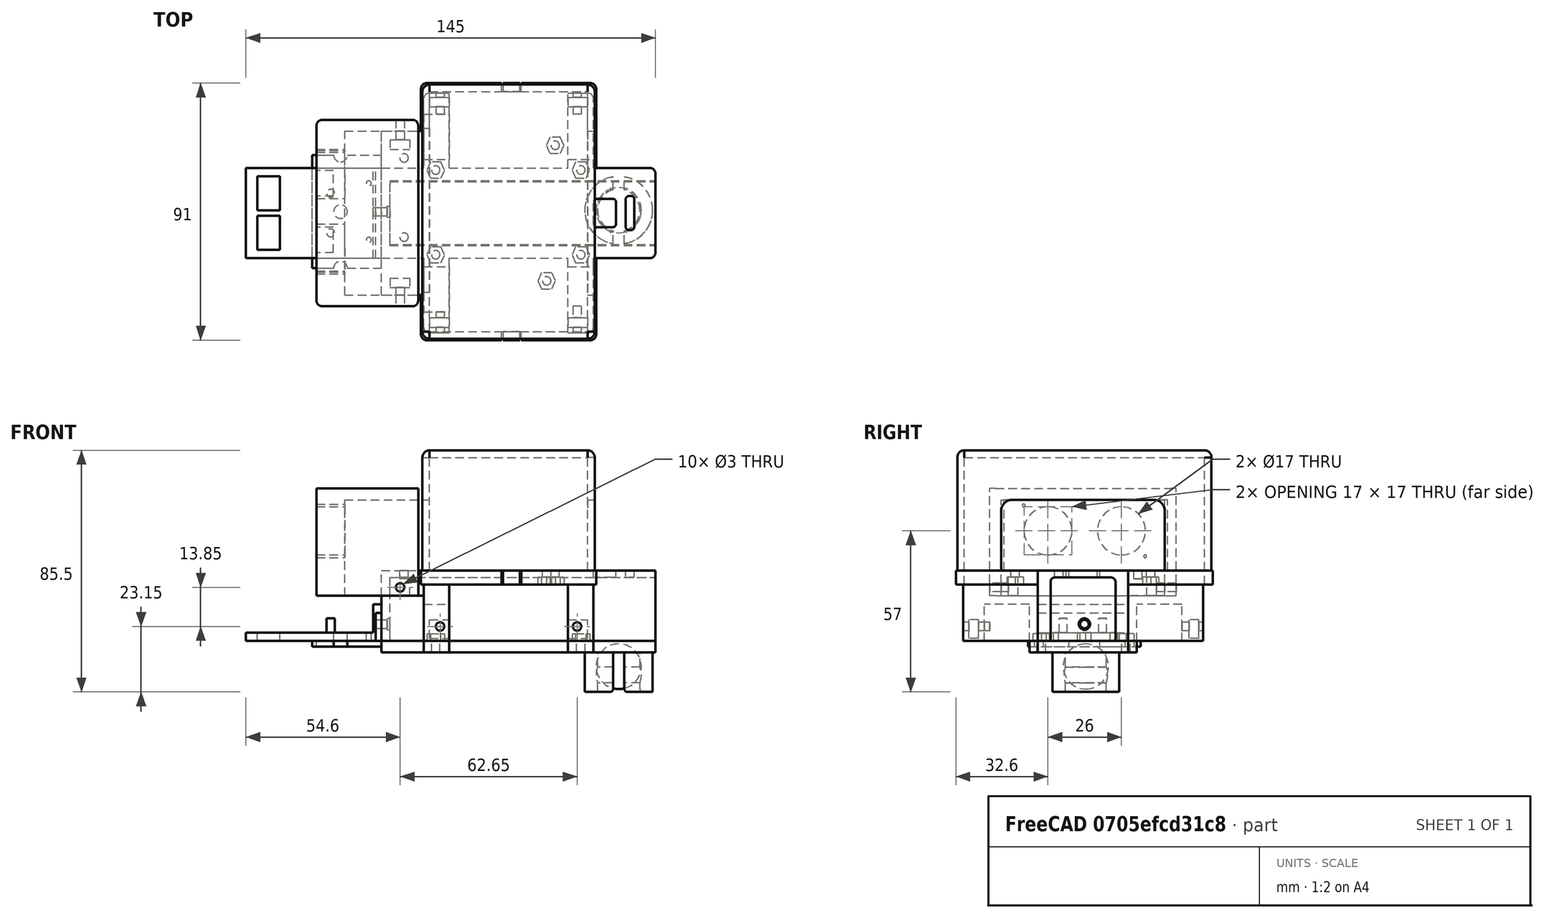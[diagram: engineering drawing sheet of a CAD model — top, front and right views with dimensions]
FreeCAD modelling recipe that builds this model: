
FCSTD DOCUMENT  (FreeCAD 0.14R3700 (Git))
Label: startRobot_v2
License: CC-BY 3.0
LicenseURL: http://creativecommons.org/licenses/by/3.0/
objects: Part::Cut×56, Part::Box×45, Part::Cylinder×33, Part::MultiFuse×15, Part::Fillet×9, Part::Offset×9, Mesh::Feature×7, PartDesign::Pad×7, Part::Feature×4, Part::Sphere×3, Part::Thickness×1, Sketcher::SketchObject×1
note: 190 computed .brp shape members not serialized (recipe doc carries the construction recipe); baked Part::Feature solids carry a one-line shape summary decoded from their .brp

FEATURE [Mesh::Feature] powerBank
  Placement = pos=(52,10,0) rot=(0,0,1;3.14159rad)
FEATURE [Part::Box] Box  label="Cubo"
  Height = 25
  Length = 94
  Placement = pos=(-42,-17,0) rot=(0,0,1;0rad)
  Width = 32
FEATURE [Part::Box] Box001  label="Cubo001"
  Height = 22
  Length = 94
  Placement = pos=(-42,-12,0) rot=(0,0,1;0rad)
  Width = 22
FEATURE [Part::Fillet] Fillet
  Base = -> Box001
  Edges = 4 edges r=1: [Edge9,Edge10,Edge11,Edge12]
FEATURE [Part::Offset] Offset
  Fill = false
  Intersection = false
  Join = 0
  Mode = 0
  SelfIntersection = false
  Source = -> Fillet
  Value = 0.5
FEATURE [Part::Cut] Cut
  Base = -> Box
  Tool = -> Offset
FEATURE [Part::Feature] futaba  label="Right-servo001"
  Placement = pos=(0,-17,10) rot=(0,0,1;0rad)
  shape: bbox 55.3 x 42 x 20 mm, 163 faces, 0 solids (baked)
FEATURE [Part::Feature] futaba001  label="Left-servo001"
  Placement = pos=(0,15,10) rot=(0,0,1;0rad)
  shape: bbox 55.3 x 42 x 20 mm, 163 faces, 0 solids (baked)
FEATURE [Part::Box] Box002  label="Cubo002"
  Height = 5
  Length = 62
  Placement = pos=(-31,-46,20) rot=(0,0,1;0rad)
  Width = 29
FEATURE [Part::Box] Box003  label="Cubo003"
  Height = 5
  Length = 62
  Placement = pos=(-31,15,20) rot=(0,0,1;0rad)
  Width = 30
FEATURE [Part::MultiFuse] Fusion
  Shapes = -> [Cut,Box002,Box003]
FEATURE [Part::Box] Box004  label="Cubo004"
  Height = 20
  Length = 9
  Placement = pos=(21,-43.4,0) rot=(0,0,1;0rad)
  Width = 27
FEATURE [Part::MultiFuse] Fusion001
  Shapes = -> [Fusion,Box004]
FEATURE [Part::Box] Box006  label="Cubo006"
  Height = 20
  Length = 9
  Placement = pos=(21,14.5,0) rot=(0,0,1;0rad)
  Width = 27
FEATURE [Part::MultiFuse] Fusion002
  Shapes = -> [Fusion001,Box006]
FEATURE [Part::Box] Box007  label="Cubo007"
  Height = 20
  Length = 9
  Placement = pos=(-30,14.5,0) rot=(0,0,1;0rad)
  Width = 27
FEATURE [Part::Box] Box008  label="Cubo008"
  Height = 20
  Length = 9
  Placement = pos=(-30,-43.4,0) rot=(0,0,1;0rad)
  Width = 27
FEATURE [Part::MultiFuse] Fusion003
  Shapes = -> [Fusion002,Box008]
FEATURE [Part::MultiFuse] Fusion004
  Shapes = -> [Fusion003,Box007]
FEATURE [Mesh::Feature] hc_sr  label="hc-sr04"
  Placement = pos=(-57,22,29) rot=(0.57735,-0.57735,-0.57735;2.0944rad)
FEATURE [Part::Box] Box010  label="Cubo010"
  Height = 25
  Length = 3
  Placement = pos=(-45,-17,0) rot=(0,0,1;0rad)
  Width = 32
FEATURE [Part::MultiFuse] Fusion005
  Shapes = -> [Box010,Fusion004]
FEATURE [Mesh::Feature] baseArduino
  Placement = pos=(-4,-1,30) rot=(0,0,1;1.5708rad)
FEATURE [Part::Box] Box011  label="Cubo011"
  Height = 4
  Length = 36
  Placement = pos=(-62,-34,50) rot=(0,0,1;0rad)
  Width = 66
FEATURE [Part::Box] Box012  label="Cubo012"
  Height = 34
  Length = 10
  Placement = pos=(-62,-34,16) rot=(0,0,1;0rad)
  Width = 66
FEATURE [Part::Box] Box013  label="Cubo013"
  Height = 9
  Length = 17
  Placement = pos=(-45,15,16) rot=(0,0,1;0rad)
  Width = 13
FEATURE [Part::Box] Box014  label="Cubo014"
  Height = 34
  Length = 26
  Placement = pos=(-52,28,16) rot=(0,0,1;0rad)
  Width = 4
FEATURE [Part::Box] Box015  label="huecoTuerca"
  Height = 3.4
  Length = 7
  Placement = pos=(-42,25,16) rot=(1,0,0;1.5708rad)
  Width = 6.5
FEATURE [Part::Box] Box016  label="huecoTuerca001"
  Height = 3.4
  Length = 7
  Placement = pos=(-28,40,1) rot=(1,0,0;1.5708rad)
  Width = 6.5
FEATURE [Part::Box] Box017  label="Cubo015"
  Height = 34
  Length = 26
  Placement = pos=(-52,-34,16) rot=(0,0,1;0rad)
  Width = 4
FEATURE [Part::Box] Box018  label="Cubo016"
  Height = 9
  Length = 17
  Placement = pos=(-45,-30,16) rot=(0,0,1;0rad)
  Width = 13
FEATURE [Part::Box] Box019  label="huecoTuerca002"
  Height = 3.4
  Length = 7
  Placement = pos=(-42,-24,16) rot=(1,0,0;1.5708rad)
  Width = 6.5
FEATURE [Part::MultiFuse] Fusion006  label="cabeza"
  Shapes = -> [Box011,Box012,Box014,Box017]
FEATURE [Part::MultiFuse] Fusion007
  Shapes = -> [Fusion005,Box013,Box018]
FEATURE [Part::Cut] Cut001
  Base = -> Fusion007
  Tool = -> Box015
FEATURE [Part::Cut] Cut002
  Base = -> Cut001
  Tool = -> Box019
FEATURE [Part::Box] Box020  label="huecoTuerca003"
  Height = 3.4
  Length = 7
  Placement = pos=(-28,-38,1) rot=(1,0,0;1.5708rad)
  Width = 6.5
FEATURE [Part::Cut] Cut003
  Base = -> Cut002
  Tool = -> Box016
FEATURE [Part::Cut] Cut004
  Base = -> Cut003
  Tool = -> Box020
FEATURE [Part::Box] Box021  label="huecoTuerca004"
  Height = 3.4
  Length = 7
  Placement = pos=(21,40,1) rot=(1,0,0;1.5708rad)
  Width = 6.5
FEATURE [Part::Box] Box022  label="huecoTuerca005"
  Height = 3.4
  Length = 7
  Placement = pos=(21,-38,1) rot=(1,0,0;1.5708rad)
  Width = 6.5
FEATURE [Part::Cut] Cut005
  Base = -> Cut004
  Tool = -> Box021
FEATURE [Part::Cut] Cut006
  Base = -> Cut005
  Tool = -> Box022
FEATURE [Part::Cylinder] Cylinder  label="Cilindro"
  Angle = 360
  Height = 10
  Placement = pos=(24.25,44,5.15) rot=(1,0,0;1.5708rad)
  Radius = 1.5
FEATURE [Part::Cylinder] Cylinder001  label="Cilindro001"
  Angle = 360
  Height = 10
  Placement = pos=(-24.25,44,5.15) rot=(1,0,0;1.5708rad)
  Radius = 1.5
FEATURE [Part::Cylinder] Cylinder002  label="Cilindro002"
  Angle = 360
  Height = 10
  Placement = pos=(24.25,-34,5.15) rot=(1,0,0;1.5708rad)
  Radius = 1.5
FEATURE [Part::Cylinder] Cylinder003  label="Cilindro003"
  Angle = 360
  Height = 10
  Placement = pos=(-24.25,-34,5.15) rot=(1,0,0;1.5708rad)
  Radius = 1.5
FEATURE [Part::Cut] Cut007
  Base = -> Cut006
  Tool = -> Cylinder
FEATURE [Part::Cut] Cut008
  Base = -> Cut007
  Tool = -> Cylinder001
FEATURE [Part::Cut] Cut009
  Base = -> Cut008
  Tool = -> Cylinder003
FEATURE [Part::Cut] Cut010
  Base = -> Cut009
  Tool = -> Cylinder002
FEATURE [Part::Box] Box023  label="Cubo017"
  Height = 13
  Length = 11
  Placement = pos=(-31,18,0) rot=(0,0,1;0rad)
  Width = 16
FEATURE [Part::Box] Box024  label="Cubo018"
  Height = 13
  Length = 11
  Placement = pos=(-31,-36,0) rot=(0,0,1;0rad)
  Width = 16
FEATURE [Part::Cut] Cut011
  Base = -> Cut010
  Tool = -> Box023
FEATURE [Part::Cut] Cut012
  Base = -> Cut011
  Tool = -> Box024
FEATURE [Part::Cylinder] Cylinder004  label="Cilindro004"
  Angle = 360
  Height = 10
  Placement = pos=(-38.4,-24,19) rot=(1,0,0;1.5708rad)
  Radius = 1.5
FEATURE [Part::Cylinder] Cylinder005  label="Cilindro005"
  Angle = 360
  Height = 10
  Placement = pos=(-38.4,32,19) rot=(1,0,0;1.5708rad)
  Radius = 1.5
FEATURE [Part::Cylinder] Cylinder006  label="Cilindro006"
  Angle = 360
  Height = 10
  Placement = pos=(-32.4,-24,19) rot=(1,0,0;1.5708rad)
  Radius = 1.5
FEATURE [Part::Cylinder] Cylinder007  label="Cilindro007"
  Angle = 360
  Height = 10
  Placement = pos=(-32.4,32,19) rot=(1,0,0;1.5708rad)
  Radius = 1.5
FEATURE [Part::Cut] Cut013
  Base = -> Cut012
  Tool = -> Cylinder004
FEATURE [Part::Cut] Cut014
  Base = -> Cut013
  Tool = -> Cylinder005
FEATURE [Part::Cut] Cut015
  Base = -> Fusion006
  Tool = -> Cylinder006
FEATURE [Part::Cut] Cut016
  Base = -> Cut015
  Tool = -> Cylinder007
FEATURE [Part::Box] Box025  label="Cubo019"
  Height = 4
  Length = 97
  Placement = pos=(-45,-17,-4) rot=(0,0,1;0rad)
  Width = 32
FEATURE [PartDesign::Pad] Pad  label="tuercaM015"
  Length = 2.4
  Length2 = 100
  Placement = pos=(-24.2,25,14.8) rot=(1,0,0;1.5708rad)
  Type = 0
FEATURE [Part::Offset] Offset001  label="tuercaM014"
  Fill = false
  Intersection = false
  Join = 2
  Mode = 0
  Placement = pos=(-1.6,-1,-22.5) rot=(1,0,0;1.5708rad)
  SelfIntersection = false
  Source = -> Pad
  Value = 0.1
FEATURE [PartDesign::Pad] Pad001  label="tuercaM017"
  Length = 2.4
  Length2 = 100
  Placement = pos=(-24.2,25,14.8) rot=(1,0,0;1.5708rad)
  Type = 0
FEATURE [Part::Offset] Offset002  label="tuercaM016"
  Fill = false
  Intersection = false
  Join = 2
  Mode = 0
  Placement = pos=(-1.6,29,-22.5) rot=(1,0,0;1.5708rad)
  SelfIntersection = false
  Source = -> Pad001
  Value = 0.1
FEATURE [Part::Cut] Cut017
  Base = -> Cut014
  Tool = -> Offset001
FEATURE [Part::Cut] Cut018
  Base = -> Cut017
  Tool = -> Offset002
FEATURE [Part::Box] Box026  label="Cubo020"
  Height = 4
  Length = 9
  Placement = pos=(-30,15,-4) rot=(0,0,1;0rad)
  Width = 3
FEATURE [Part::Box] Box027  label="Cubo021"
  Height = 4
  Length = 9
  Placement = pos=(-30,-20,-4) rot=(0,0,1;0rad)
  Width = 3
FEATURE [Part::MultiFuse] Fusion008
  Shapes = -> [Box025,Box026,Box027]
FEATURE [PartDesign::Pad] Pad002  label="tuercaM019"
  Length = 2.4
  Length2 = 100
  Placement = pos=(-24.2,25,14.8) rot=(1,0,0;1.5708rad)
  Type = 0
FEATURE [Part::Offset] Offset003  label="tuercaM018"
  Fill = false
  Intersection = false
  Join = 2
  Mode = 0
  Placement = pos=(49.8,29,-22.5) rot=(1,0,0;1.5708rad)
  SelfIntersection = false
  Source = -> Pad002
  Value = 0.1
FEATURE [PartDesign::Pad] Pad003  label="tuercaM021"
  Length = 2.4
  Length2 = 100
  Placement = pos=(-24.2,25,14.8) rot=(1,0,0;1.5708rad)
  Type = 0
FEATURE [Part::Offset] Offset004  label="tuercaM020"
  Fill = false
  Intersection = false
  Join = 2
  Mode = 0
  Placement = pos=(49.8,-1,-22.5) rot=(1,0,0;1.5708rad)
  SelfIntersection = false
  Source = -> Pad003
  Value = 0.1
FEATURE [Part::Cut] Cut019
  Base = -> Cut018
  Tool = -> Offset003
FEATURE [Part::Cut] Cut020
  Base = -> Cut019
  Tool = -> Offset004
FEATURE [Part::Box] Box028  label="Cubo022"
  Height = 4
  Length = 9
  Placement = pos=(21,15,-4) rot=(0,0,1;0rad)
  Width = 3
FEATURE [Part::Box] Box029  label="Cubo023"
  Height = 4
  Length = 9
  Placement = pos=(21,-20,-4) rot=(0,0,1;0rad)
  Width = 3
FEATURE [Part::MultiFuse] Fusion009
  Shapes = -> [Fusion008,Box028,Box029]
FEATURE [Part::Cylinder] Cylinder008  label="Cilindro008"
  Angle = 360
  Height = 6
  Placement = pos=(25.6,14.25,-4) rot=(0,0,1;0rad)
  Radius = 1.5
FEATURE [Part::Cylinder] Cylinder009  label="Cilindro009"
  Angle = 360
  Height = 6
  Placement = pos=(25.6,-15.75,-4) rot=(0,0,1;0rad)
  Radius = 1.5
FEATURE [Part::Cylinder] Cylinder010  label="Cilindro010"
  Angle = 360
  Height = 6
  Placement = pos=(-25.8,-15.75,-4) rot=(0,0,1;0rad)
  Radius = 1.5
FEATURE [Part::Cylinder] Cylinder011  label="Cilindro011"
  Angle = 360
  Height = 6
  Placement = pos=(-25.8,14.25,-4) rot=(0,0,1;0rad)
  Radius = 1.5
FEATURE [Part::Cut] Cut021
  Base = -> Fusion009
  Tool = -> Cylinder008
FEATURE [Part::Cut] Cut022
  Base = -> Cut021
  Tool = -> Cylinder011
FEATURE [Part::Cut] Cut023
  Base = -> Cut022
  Tool = -> Cylinder010
FEATURE [Part::Cut] Cut024  label="baseBateria"
  Base = -> Cut023
  Tool = -> Cylinder009
FEATURE [Part::Box] Box030  label="Cubo024"
  Height = 10
  Length = 8
  Placement = pos=(30,-6,19) rot=(0,0,1;0rad)
  Width = 10
FEATURE [Part::Fillet] Fillet001
  Base = -> Box030
  Edges = 4 edges r=1: [Edge1,Edge3,Edge5,Edge7]
FEATURE [Part::Box] Box031  label="Cubo025"
  Height = 10
  Length = 3
  Placement = pos=(41.5,-7,20) rot=(0,0,1;0rad)
  Width = 12
FEATURE [Part::Fillet] Fillet002
  Base = -> Box031
  Edges = 4 edges r=1: [Edge1,Edge3,Edge5,Edge7]
FEATURE [Part::Cut] Cut025
  Base = -> Cut020
  Tool = -> Fillet001
FEATURE [Part::Cut] Cut026
  Base = -> Cut025
  Tool = -> Fillet002
FEATURE [Part::Fillet] Fillet003
  Base = -> Cut026
  Edges = 10 edges r=2: [Edge86,Edge87,Edge180,Edge190,Edge231,Edge243,Edge350,Edge351,Edge352,Edge353]
FEATURE [Part::Feature] Servo_wheel_4_arm_horn  label="Servo_wheel_4_arm_horn003"
  Placement = pos=(1,-17,10) rot=(0,0,1;0rad)
  shape: bbox 56 x 6 x 56 mm, 1285 faces, 0 solids (baked)
FEATURE [Part::Feature] Servo_wheel_4_arm_horn001  label="Servo_wheel_4_arm_horn004"
  Placement = pos=(0,14,10) rot=(0,0,1;0rad)
  shape: bbox 56 x 6 x 56 mm, 1286 faces, 0 solids (baked)
FEATURE [PartDesign::Pad] Pad004  label="tuercaM023"
  Length = 2.4
  Length2 = 100
  Placement = pos=(-24.2,25,14.8) rot=(1,0,0;1.5708rad)
  Type = 0
FEATURE [Part::Offset] Offset005  label="tuercaM022"
  Fill = false
  Intersection = false
  Join = 2
  Mode = 0
  Placement = pos=(37.7,-10.2,-2.5) rot=(1,0,0;1.5708rad)
  SelfIntersection = false
  Source = -> Pad004
  Value = 0.1
FEATURE [Part::Cylinder] Cylinder013  label="Cilindro013"
  Angle = 360
  Height = 15
  Placement = pos=(-37,18.5,22) rot=(0,0,1;0rad)
  Radius = 1.5
FEATURE [Part::Cylinder] Cylinder014  label="Cilindro014"
  Angle = 360
  Height = 42
  Placement = pos=(13.5,-25,-3) rot=(0,0,1;0rad)
  Radius = 1.5
FEATURE [Part::Cylinder] Cylinder015  label="Cilindro015"
  Angle = 360
  Height = 42
  Placement = pos=(16.5,23,-3) rot=(0,0,1;0rad)
  Radius = 1.5
FEATURE [PartDesign::Pad] Pad005  label="tuercaM025"
  Length = 2.4
  Length2 = 100
  Placement = pos=(-24.2,25,14.8) rot=(1,0,0;1.5708rad)
  Type = 0
FEATURE [Part::Offset] Offset006  label="tuercaM024"
  Fill = false
  Intersection = false
  Join = 2
  Mode = 0
  Placement = pos=(40.7,37.8,-2.5) rot=(1,0,0;1.5708rad)
  SelfIntersection = false
  Source = -> Pad005
  Value = 0.1
FEATURE [Part::Cut] Cut027
  Base = -> Fillet003
  Tool = -> Offset005
FEATURE [Part::Cut] Cut028
  Base = -> Cut027
  Tool = -> Offset006
FEATURE [Part::Cut] Cut029
  Base = -> Cut028
  Tool = -> Cylinder015
FEATURE [Part::Cut] Cut030
  Base = -> Cut029
  Tool = -> Cylinder014
FEATURE [Part::Cut] Cut031
  Base = -> Cut030
  Tool = -> Cylinder013
FEATURE [Part::Cylinder] Cylinder016  label="Cilindro016"
  Angle = 360
  Height = 15
  Placement = pos=(-37,-9.5,22) rot=(0,0,1;0rad)
  Radius = 1.5
FEATURE [Part::Cut] Cut032
  Base = -> Cut031
  Tool = -> Cylinder016
FEATURE [Part::Cylinder] Cylinder017  label="Cilindro017"
  Angle = 360
  Height = 15
  Placement = pos=(-64,-13.4,39) rot=(0,1,0;1.5708rad)
  Radius = 8
FEATURE [Part::Cylinder] Cylinder018  label="Cilindro018"
  Angle = 360
  Height = 15
  Placement = pos=(-64,12.6,39) rot=(0,1,0;1.5708rad)
  Radius = 8
FEATURE [Part::Offset] Offset007
  Fill = false
  Intersection = false
  Join = 0
  Mode = 0
  SelfIntersection = false
  Source = -> Cylinder017
  Value = 0.5
FEATURE [Part::Offset] Offset008
  Fill = false
  Intersection = false
  Join = 0
  Mode = 0
  SelfIntersection = false
  Source = -> Cylinder018
  Value = 0.5
FEATURE [Part::Cut] Cut033
  Base = -> Cut016
  Tool = -> Offset007
FEATURE [Part::Cut] Cut034
  Base = -> Cut033
  Tool = -> Offset008
FEATURE [Part::Cylinder] Cylinder019  label="Cilindro019"
  Angle = 360
  Height = 15
  Placement = pos=(-63,-22,48) rot=(0,1,0;1.5708rad)
  Radius = 0.5
FEATURE [Part::Cylinder] Cylinder020  label="Cilindro020"
  Angle = 360
  Height = 15
  Placement = pos=(-65,21,30) rot=(0,1,0;1.5708rad)
  Radius = 0.5
FEATURE [Part::Cut] Cut035
  Base = -> Cut034
  Tool = -> Cylinder019
FEATURE [Part::Cut] Cut036
  Base = -> Cut035
  Tool = -> Cylinder020
FEATURE [Part::Fillet] Fillet004  label="CabezaRobot"
  Base = -> Cut036
  Edges = 4 edges r=2: [Edge13,Edge14,Edge18,Edge19]
  Placement = pos=(-6,0,0) rot=(0,0,1;0rad)
FEATURE [Part::Cylinder] Cylinder021  label="Cilindro021"
  Angle = 360
  Height = 14
  Placement = pos=(39,0,-18) rot=(0,0,1;0rad)
  Radius = 12
FEATURE [Part::Sphere] Sphere  label="Esféra"
  Angle1 = -90
  Angle2 = 90
  Angle3 = 360
  Placement = pos=(39,0,-12) rot=(0,0,1;0rad)
  Radius = 8
FEATURE [Part::Box] Box032  label="Cubo026"
  Height = 16
  Length = 4
  Placement = pos=(37,-12,-19) rot=(0,0,1;0rad)
  Width = 6
FEATURE [Part::Box] Box033  label="Cubo027"
  Height = 16
  Length = 4
  Placement = pos=(37,6,-19) rot=(0,0,1;0rad)
  Width = 6
FEATURE [Part::Sphere] Sphere001  label="Esféra001"
  Angle1 = -90
  Angle2 = 90
  Angle3 = 360
  Placement = pos=(39,0,-12) rot=(0,0,1;0rad)
  Radius = 8
FEATURE [Part::Cut] Cut040
  Base = -> Cut024
  Tool = -> Sphere001
FEATURE [Part::Sphere] Sphere002  label="Esféra002"
  Angle1 = -90
  Angle2 = 90
  Angle3 = 360
  Placement = pos=(39,0,-9) rot=(0,0,1;0rad)
  Radius = 8
FEATURE [Part::Cylinder] Cylinder022  label="Cilindro022"
  Angle = 360
  Height = 14
  Placement = pos=(39,0,-18) rot=(0,0,1;0rad)
  Radius = 7.5
FEATURE [Part::Cut] Cut041
  Base = -> Cylinder021
  Tool = -> Cylinder022
FEATURE [Part::Cut] Cut042
  Base = -> Cut041
  Tool = -> Box033
FEATURE [Part::Cut] Cut043
  Base = -> Cut042
  Tool = -> Box032
FEATURE [Part::Cut] Cut044
  Base = -> Cut043
  Tool = -> Sphere
FEATURE [Part::Fillet] Fillet005
  Base = -> Cut044
  Edges = 3 edges r=1: [Edge5,Edge6,Edge7]
FEATURE [Part::Fillet] Fillet006
  Base = -> Fillet005
  Edges = 4 edges r=1: [Edge39,Edge41,Edge42,Edge43]
FEATURE [Part::MultiFuse] Fusion010  label="tapaV1"
  Shapes = -> [Cut040,Fillet006]
FEATURE [Part::Box] Box034  label="Cubo028"
  Height = 40
  Length = 56
  Placement = pos=(-31,-46,38) rot=(0,0,1;0rad)
  Width = 85
FEATURE [Part::Thickness] Thickness
  Faces = -> Box034 [Face5]
  Intersection = false
  Join = 0
  Mode = 0
  Placement = pos=(2,2,-13) rot=(0,0,1;0rad)
  SelfIntersection = false
  Value = 2.5
FEATURE [Part::Box] Box035  label="Cubo029"
  Height = 25
  Length = 10
  Placement = pos=(-36,-30,25) rot=(0,0,1;0rad)
  Width = 58
FEATURE [Part::Cut] Cut045
  Base = -> Thickness
  Placement = pos=(1,1,0) rot=(0,0,1;0rad)
  Tool = -> Box035
FEATURE [Sketcher::SketchObject] Sketch
  ExternalGeometry = -> [Cut045]
  Placement = pos=(1,1,25) rot=(1,0,0;3.14159rad)
  Support = -> Cut045 [Face5]
  sketch-geometry (8):
    g0: LineSegment StartX=-3 StartY=47 StartZ=0 EndX=3 EndY=47 EndZ=0
    g1: LineSegment StartX=3 StartY=47 StartZ=0 EndX=3 EndY=44 EndZ=0
    g2: LineSegment StartX=3 StartY=44 StartZ=0 EndX=-3 EndY=44 EndZ=0
    g3: LineSegment StartX=-3 StartY=44 StartZ=0 EndX=-3 EndY=47 EndZ=0
    g4: LineSegment StartX=-3 StartY=-41 StartZ=0 EndX=3 EndY=-41 EndZ=0
    g5: LineSegment StartX=3 StartY=-41 StartZ=0 EndX=3 EndY=-44 EndZ=0
    g6: LineSegment StartX=3 StartY=-44 StartZ=0 EndX=-3 EndY=-44 EndZ=0
    g7: LineSegment StartX=-3 StartY=-44 StartZ=0 EndX=-3 EndY=-41 EndZ=0
  constraints (24):
    c: Coincident(g0,g1)
    c: Coincident(g1,g2)
    c: Coincident(g2,g3)
    c: Coincident(g3,g0)
    c: Horizontal(g0)
    c: Horizontal(g2)
    c: Vertical(g1)
    c: Vertical(g3)
    c: Symmetric(g2,g1,g-2)
    c: DistanceY(g1) = -3
    c: DistanceX(g0) = 6
    c: Coincident(g4,g5)
    c: Coincident(g5,g6)
    c: Coincident(g6,g7)
    c: Coincident(g7,g4)
    c: Horizontal(g4)
    c: Horizontal(g6)
    c: Vertical(g5)
    c: Vertical(g7)
    c: Symmetric(g4,g4,g-2)
    c: DistanceX(g6) = -6
    c: DistanceY(g5) = -3
    c: PointOnObject(g4,g-3)
    c: PointOnObject(g2,g-4)
FEATURE [Part::Box] Box036  label="Cubo030"
  Height = 7
  Length = 7
  Placement = pos=(-2.5,42,18) rot=(0,0,1;0rad)
  Width = 3
FEATURE [Part::Box] Box037  label="Cubo031"
  Height = 7
  Length = 7
  Placement = pos=(-2.5,-46,18) rot=(0,0,1;0rad)
  Width = 3
FEATURE [PartDesign::Pad] Pad006
  Length = 5
  Length2 = 100
  Placement = pos=(1,1,0) rot=(0,0,1;0rad)
  Sketch = -> Sketch
  Type = 0
FEATURE [Part::Cut] Cut046
  Base = -> Cut032
  Tool = -> Box036
FEATURE [Part::Cut] Cut047
  Base = -> Cut046
  Tool = -> Box037
FEATURE [Part::Box] Box038  label="Cubo032"
  Height = 25
  Length = 10
  Placement = pos=(23,-30,25) rot=(0,0,1;0rad)
  Width = 58
FEATURE [Part::Fillet] Fillet007
  Base = -> Box038
  Edges = 2 edges r=4: [Edge10,Edge12]
FEATURE [Part::Cut] Cut048  label="CubiertaRobot"
  Base = -> Pad006
  Tool = -> Fillet007
FEATURE [Part::Fillet] Fillet008  label="TapaBateria"
  Base = -> Fusion010
  Edges = 2 edges r=2: [Edge1,Edge3]
FEATURE [Mesh::Feature] LineFinder
  Placement = pos=(-69.5,-0.5,0) rot=(0,0,-1;1.5708rad)
FEATURE [Part::Box] Box039  label="Cubo033"
  Height = 2
  Length = 24.5
  Placement = pos=(-69.5,-20.5,-2) rot=(0,0,1;0rad)
  Width = 40
FEATURE [Mesh::Feature] LineFinder001
  Placement = pos=(-69.5,19.5,0) rot=(0,0,-1;1.5708rad)
FEATURE [Part::Box] Box040  label="Cubo034"
  Height = 10
  Length = 6
  Placement = pos=(-68,-15,-3) rot=(0,0,1;0rad)
  Width = 9
FEATURE [Part::Box] Box041  label="Cubo035"
  Height = 10
  Length = 6
  Placement = pos=(-68,5,-3) rot=(0,0,1;0rad)
  Width = 9
FEATURE [Part::Cut] Cut049
  Base = -> Box039
  Tool = -> Box040
FEATURE [Part::Cut] Cut050
  Base = -> Cut049
  Tool = -> Box041
FEATURE [Part::Box] Box042  label="Cubo036"
  Height = 10
  Length = 2
  Placement = pos=(-47,-17,0) rot=(0,0,1;0rad)
  Width = 32
FEATURE [Part::MultiFuse] Fusion011
  Shapes = -> [Cut050,Box042]
FEATURE [Part::Cylinder] Cylinder023  label="Cilindro023"
  Angle = 360
  Height = 3
  Placement = pos=(-59.5,-0.5,0) rot=(0,0,1;0rad)
  Radius = 2.4
FEATURE [Part::Cylinder] Cylinder024  label="Cilindro024"
  Angle = 360
  Height = 5
  Placement = pos=(-59.5,19.5,-3) rot=(0,0,1;0rad)
  Radius = 2.4
FEATURE [Part::Cylinder] Cylinder025  label="Cilindro025"
  Angle = 360
  Height = 6
  Placement = pos=(-59.5,-20.5,-4) rot=(0,0,1;0rad)
  Radius = 2.4
FEATURE [Part::Cut] Cut051
  Base = -> Fusion011
  Tool = -> Cylinder024
FEATURE [Part::Cut] Cut052
  Base = -> Cut051
  Tool = -> Cylinder025
FEATURE [Part::Cylinder] Cylinder026  label="Cilindro026"
  Angle = 360
  Height = 3
  Placement = pos=(-49.5,9.5,0) rot=(0,0,1;0rad)
  Radius = 0.9
FEATURE [Part::Cylinder] Cylinder027  label="Cilindro027"
  Angle = 360
  Height = 3
  Placement = pos=(-49.5,-10.5,0) rot=(0,0,1;0rad)
  Radius = 0.9
FEATURE [Part::MultiFuse] Fusion012
  Shapes = -> [Cut052,Cylinder023,Cylinder026,Cylinder027]
FEATURE [Part::Cylinder] Cylinder028  label="Cilindro028"
  Angle = 360
  Height = 10
  Placement = pos=(-49,-0.5,6) rot=(0,1,0;1.5708rad)
  Radius = 1.5
FEATURE [Part::Cylinder] Cylinder029  label="Cilindro029"
  Angle = 360
  Height = 10
  Placement = pos=(-49,-0.5,6) rot=(0,1,0;1.5708rad)
  Radius = 1.5
FEATURE [Part::Cut] Cut053  label="SoporteSensoresLineFinder"
  Base = -> Fusion012
  Tool = -> Cylinder028
FEATURE [Part::Cut] Cut054
  Base = -> Cut047
  Tool = -> Cylinder029
FEATURE [Part::Cylinder] Cylinder030  label="Cilindro030"
  Angle = 360
  Height = 3
  Placement = pos=(-43,-0.5,6) rot=(0,1,0;1.5708rad)
  Radius = 2
FEATURE [Part::Cut] Cut055  label="ChasisRobot"
  Base = -> Cut054
  Tool = -> Cylinder030
FEATURE [Mesh::Feature] TCRT5000  label="TCRT5000Right"
  Placement = pos=(-88,-1,4) rot=(0.707107,0.707107,0;3.14159rad)
FEATURE [Mesh::Feature] TCRT  label="TCRT5000Left"
  Placement = pos=(-88,-15,4) rot=(0.707107,0.707107,0;3.14159rad)
FEATURE [Part::Box] Box043  label="Cubo037"
  Height = 3
  Length = 48
  Placement = pos=(-93,-17,0) rot=(0,0,1;0rad)
  Width = 32
FEATURE [Part::Box] Box044  label="Cubo038"
  Height = 13
  Length = 3
  Placement = pos=(-48,-17,0) rot=(0,0,1;0rad)
  Width = 32
FEATURE [Part::MultiFuse] Fusion013
  Shapes = -> [Box043,Box044]
FEATURE [Part::Cylinder] Cylinder031  label="Cilindro031"
  Angle = 360
  Height = 10
  Placement = pos=(-51,-0.5,6) rot=(0,1,0;1.5708rad)
  Radius = 1.5
FEATURE [Part::Cut] Cut056
  Base = -> Fusion013
  Tool = -> Cylinder031
FEATURE [Part::Box] Box045  label="Cubo039"
  Height = 10
  Length = 8
  Placement = pos=(-89,-14,-2) rot=(0,0,1;0rad)
  Width = 12
FEATURE [Part::Box] Box046  label="Cubo040"
  Height = 10
  Length = 8
  Placement = pos=(-89,0,-2) rot=(0,0,1;0rad)
  Width = 12
FEATURE [Part::Cut] Cut057
  Base = -> Cut056
  Tool = -> Box045
FEATURE [Part::Cut] Cut058
  Base = -> Cut057
  Tool = -> Box046
FEATURE [Part::Cylinder] Cylinder032  label="Cilindro032"
  Angle = 360
  Height = 5
  Placement = pos=(-63,6,3) rot=(0,0,1;0rad)
  Radius = 1.4
FEATURE [Part::Cylinder] Cylinder033  label="Cilindro033"
  Angle = 360
  Height = 5
  Placement = pos=(-63,-8,3) rot=(0,0,1;0rad)
  Radius = 1.4
FEATURE [Part::MultiFuse] Fusion014  label="soporteSensoresTCRT5000"
  Shapes = -> [Cut058,Cylinder032,Cylinder033]
